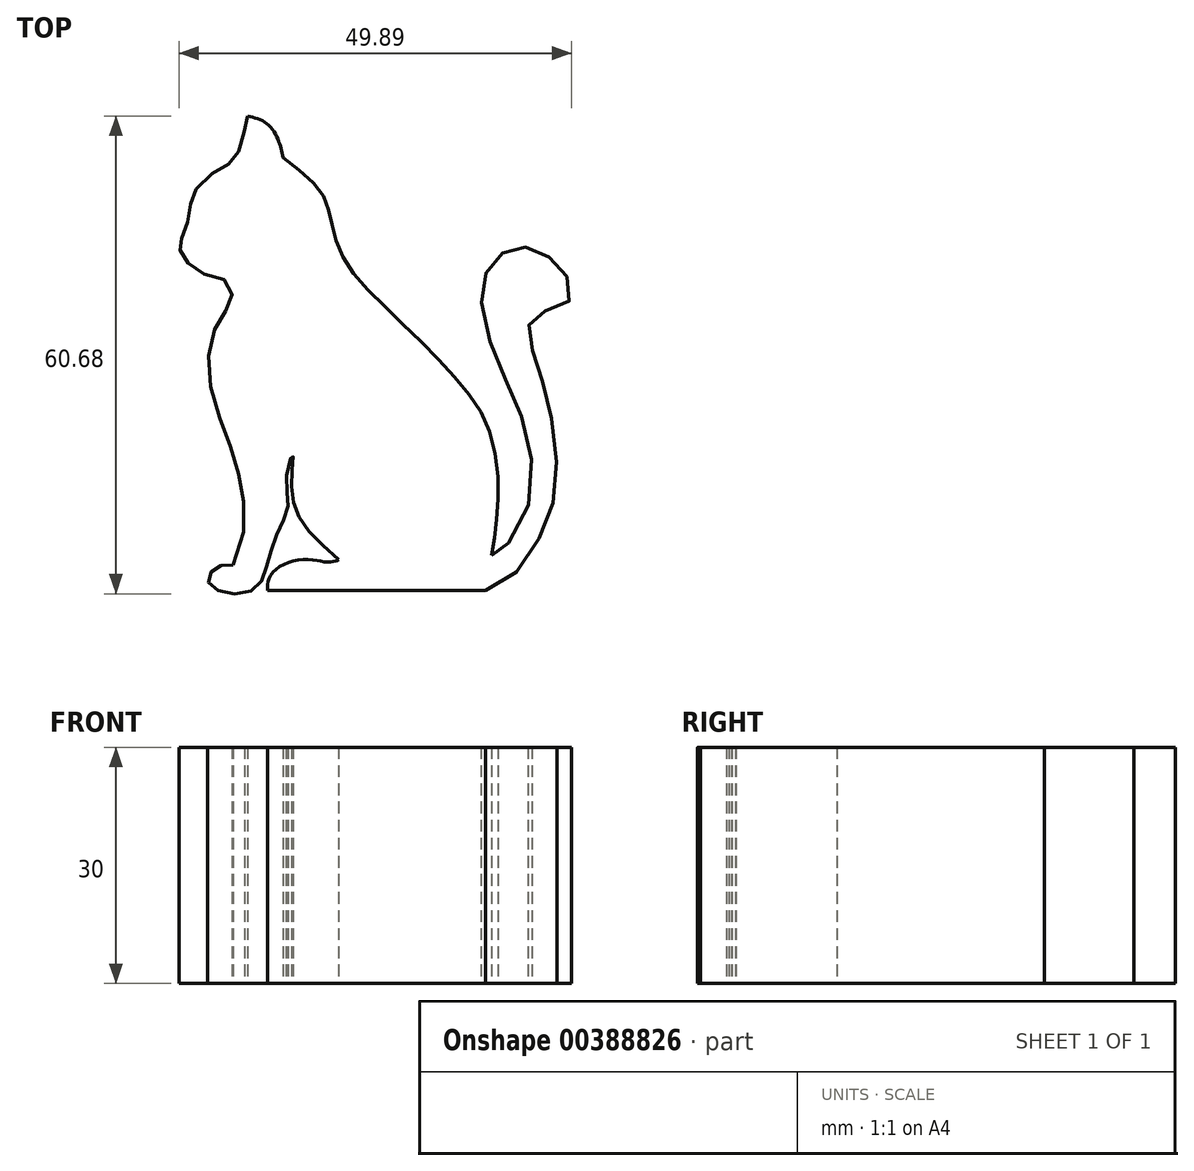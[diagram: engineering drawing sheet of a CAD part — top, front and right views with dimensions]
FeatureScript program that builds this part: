
annotation { "Feature Type Name" : "Feature", "Feature Type Description" : "" }
export const myFeature = defineFeature(function(context is Context, id is Id, definition is map)
    precondition{}
    {
        {
            var Q0;
            Q0=qCreatedBy(makeId("Top.planeOp"),FACE);
            var sketch = newSketch(context, id + "F0", { "sketchPlane" : qUnion([Q0])});
            skFitSpline(sketch, "E0", {"points": [v(-15.3, 26.6) * mm, v(-15.83, 24.18) * mm, v(-16.98, 21.07) * mm, v(-19.07, 19.79) * mm, v(-22.06, 16.95) * mm, v(-22.58, 14.86) * mm, v(-23.32, 11.76) * mm, v(-24, 10.14) * mm, v(-23.46, 8.92) * mm, v(-21.57, 6.82) * mm, v(-18, 5.68) * mm, v(-17.32, 3.25) * mm, v(-19.07, 0.4) * mm, v(-20.24, -6.15) * mm, v(-17.7, -14.74) * mm, v(-15.86, -21.56) * mm, v(-17.1, -30.39) * mm], "startDerivative": vector(-9.54, -44.5) * mm, "endDerivative": vector(-50.53, -97.71) * mm});
            skFitSpline(sketch, "E1", {"points": [v(-17.1, -30.39) * mm, v(-19.23, -30.71) * mm, v(-20.32, -32.44) * mm, v(-18.35, -33.9) * mm, v(-14.3, -33.39) * mm, v(-12.77, -30.39) * mm, v(-11.53, -26.46) * mm, v(-10.16, -22.92) * mm, v(-10.37, -19.71) * mm, v(-9.56, -16.38) * mm, v(-9.56, -17.83) * mm, v(-9.56, -21.76) * mm, v(-8.04, -25.41) * mm, v(-3.7, -29.75) * mm], "startDerivative": vector(-35.67, 1.07) * mm, "endDerivative": vector(47.01, -41.27) * mm});
            skFitSpline(sketch, "E2", {"points": [v(-3.7, -29.75) * mm, v(-4.95, -30.07) * mm, v(-7.07, -29.75) * mm, v(-10.77, -30.39) * mm, v(-12.57, -32.2) * mm, v(-12.73, -33.68) * mm], "startDerivative": vector(-7.71, -3.08) * mm, "endDerivative": vector(0.37, -8.84) * mm});
            skLineSegment(sketch, "E3", {"start": v(-12.73, -33.68) * mm, "end": v(14.97, -33.68) * mm});
            skFitSpline(sketch, "E4", {"points": [v(14.97, -33.68) * mm, v(20.8, -28.61) * mm, v(23.84, -20.88) * mm, v(23.08, -10.62) * mm, v(21.17, -3.94) * mm, v(20.43, 0) * mm, v(22.18, 1.76) * mm, v(25.64, 3.2) * mm, v(24.98, 6.74) * mm, v(22.1, 9.23) * mm, v(18.8, 9.95) * mm, v(15.91, 8.1) * mm, v(14.4, 4.2) * mm, v(16.32, -4.18) * mm, v(19.93, -12.69) * mm, v(20, -23.92) * mm, v(16.08, -29.22) * mm, v(15.6, -29.14) * mm], "startDerivative": vector(103.9, 10.16) * mm, "endDerivative": vector(-21.83, 12.98) * mm});
            skFitSpline(sketch, "E5", {"points": [v(15.72, -29.22) * mm, v(16.5, -22.98) * mm, v(15.6, -13.78) * mm, v(11.12, -6.65) * mm, v(3.29, 1.32) * mm, v(-2.81, 8.06) * mm, v(-4.64, 13.12) * mm, v(-5.87, 16.88) * mm, v(-10.8, 21.36) * mm], "startDerivative": vector(8.45, 50.31) * mm, "endDerivative": vector(-48.33, 37.56) * mm});
            skFitSpline(sketch, "E6", {"points": [v(-10.8, 21.36) * mm, v(-11.32, 23.41) * mm, v(-12.9, 25.7) * mm, v(-15.3, 26.6) * mm], "startDerivative": vector(-1.18, 6.46) * mm, "endDerivative": vector(-7.58, 1.66) * mm});
            skSolve(sketch);
        }
        {
            var Q0;
            Q0 = qSketchRegion(id + "F0", true);
            extrude(context, id + "F1", {"entities" : qUnion([Q0]), "depth" : 30 * mm});
        }
    });
